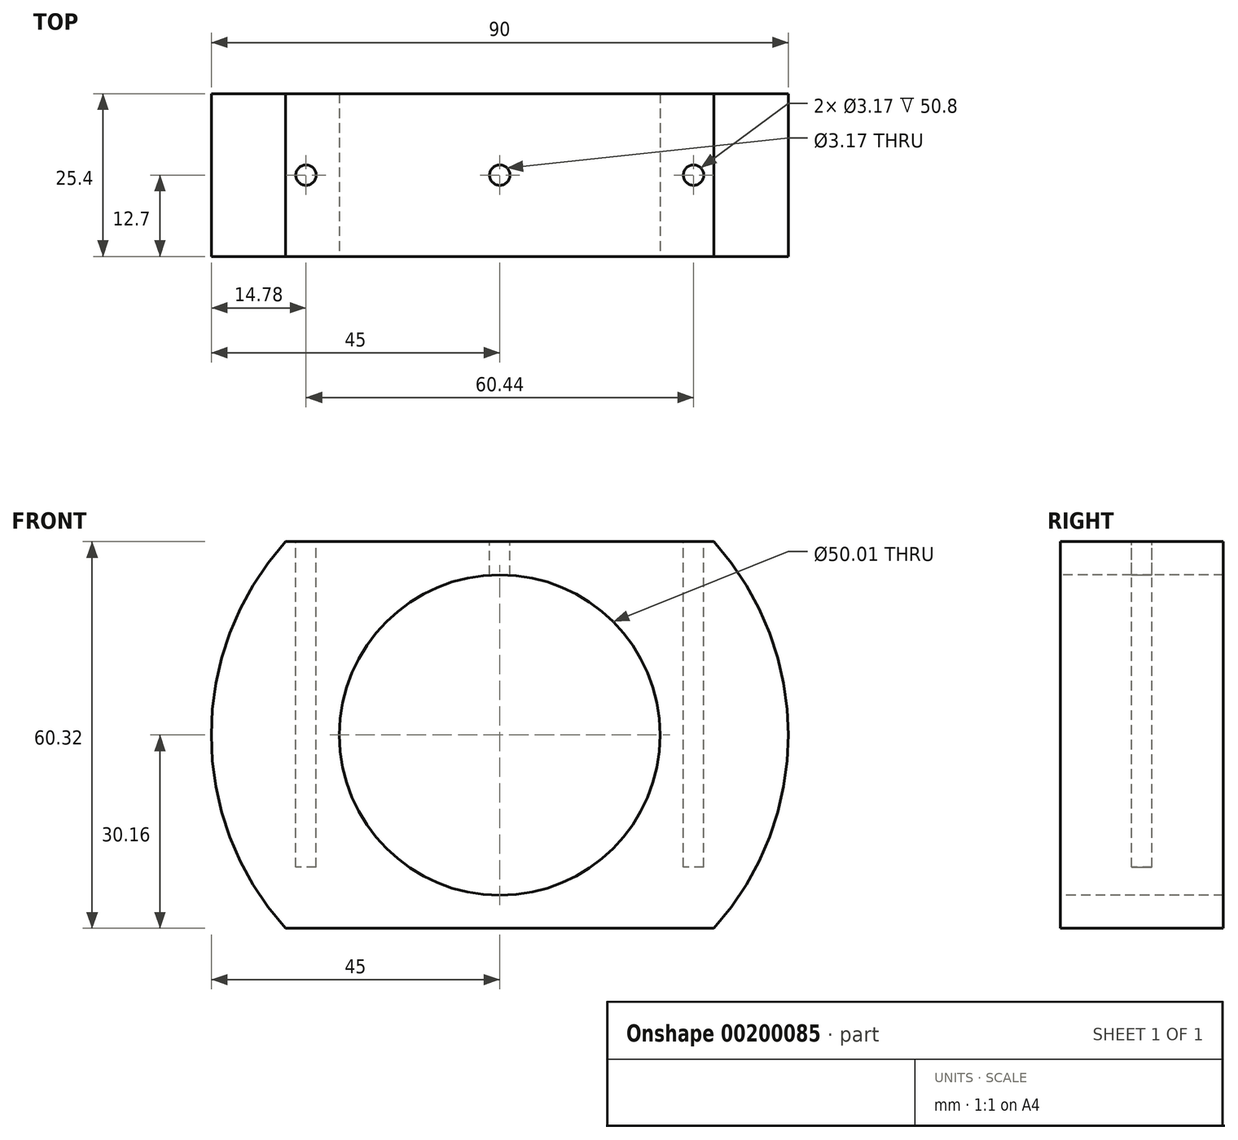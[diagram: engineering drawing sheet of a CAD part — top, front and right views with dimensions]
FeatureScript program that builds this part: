
annotation { "Feature Type Name" : "Feature", "Feature Type Description" : "" }
export const myFeature = defineFeature(function(context is Context, id is Id, definition is map)
    precondition{}
    {
        {
            var Q0;
            Q0=qCreatedBy(makeId("Front.planeOp"),FACE);
            var sketch = newSketch(context, id + "F0", { "sketchPlane" : qUnion([Q0])});
            skCircle(sketch, "E0", {"center": v(0, 0) * mm, "radius": 45 * mm});
            skSolve(sketch);
        }
        {
            var Q0;
            Q0=makeQuery(id+"F0.imprint","IMPRINT",FACE,{"disambiguationData":[TD([[makeQuery(id+"F0.imprint","IMPRINT",EDGE,{"derivedFrom":sQuery(id+"F0.wireOp",EDGE,"E0")}),1.0]])]});
            var Q1;
            Q1 = qSketchRegion(id + "F2", true);
            extrude(context, id + "F1", {"entities" : qUnion([Q0, Q1]), "endBound" : BoundingType.SYMMETRIC, "depth" : 25.4 * mm});
        }
        {
            var Q0;
            Q0=makeQuery(id+"F1.opExtrude","CAP_FACE",FACE,{"disambiguationData":[OSD([sQuery(id+"F0.wireOp",EDGE,"E0")])],"isStart":false});
            var sketch = newSketch(context, id + "F2", { "sketchPlane" : qUnion([Q0])});
            skLineSegment(sketch, "E1.bottom", {"start": v(33.4, 30.16) * mm, "end": v(-33.4, 30.16) * mm});
            skLineSegment(sketch, "E1.top", {"start": v(33.4, -30.16) * mm, "end": v(-33.4, -30.16) * mm});
            skLineSegment(sketch, "E1.left", {"start": v(33.4, 30.16) * mm, "end": v(33.4, -30.16) * mm});
            skLineSegment(sketch, "E1.right", {"start": v(-33.4, 30.16) * mm, "end": v(-33.4, -30.16) * mm});
            skPoint(sketch, "E1.middle", {"position": v(0, 0) * mm});
            skSolve(sketch);
        }
        {
            var Q0;
            {var subQ0=sQuery(id+"F2.wireOp",EDGE,"E1.bottom");Q0=makeQuery(id+"F2.imprint","IMPRINT",FACE,{"disambiguationData":[TD([[makeQuery(id+"F2.imprint","IMPRINT",EDGE,{"derivedFrom":subQ0}),-1.0]])]});}
            var Q1;
            {var subQ0=sQuery(id+"F2.wireOp",EDGE,"E1.top");Q1=makeQuery(id+"F2.imprint","IMPRINT",FACE,{"disambiguationData":[TD([[makeQuery(id+"F2.imprint","IMPRINT",EDGE,{"derivedFrom":subQ0}),1.0]])]});}
            extrude(context, id + "F3", {"entities" : qUnion([Q0, Q1]), "operationType" : NewBodyOperationType.REMOVE, "endBound" : BoundingType.THROUGH_ALL, "oppositeDirection" : true, "depth" : 25.4 * mm});
        }
        {
            var Q0;
            Q0=makeQuery(id+"F1.opExtrude","CAP_FACE",FACE,{"disambiguationData":[OSD([sQuery(id+"F0.wireOp",EDGE,"E0")])],"isStart":false});
            var sketch = newSketch(context, id + "F4", { "sketchPlane" : qUnion([Q0])});
            skCircle(sketch, "E2", {"center": v(0, 0) * mm, "radius": 25 * mm});
            skSolve(sketch);
        }
        {
            var Q0;
            Q0=makeQuery(id+"F4.imprint","IMPRINT",FACE,{"disambiguationData":[TD([[makeQuery(id+"F4.imprint","IMPRINT",EDGE,{"derivedFrom":sQuery(id+"F4.wireOp",EDGE,"E2")}),1.0]])]});
            extrude(context, id + "F5", {"entities" : qUnion([Q0]), "operationType" : NewBodyOperationType.REMOVE, "endBound" : BoundingType.THROUGH_ALL, "oppositeDirection" : true, "depth" : 25.4 * mm});
        }
        {
            var Q0;
            Q0=makeQuery(id+"F3.boolean.opBoolean","COPY",FACE,{"derivedFrom":makeQuery(id+"F3.opExtrude","SWEPT_FACE",FACE,{"disambiguationData":[OSD([sQuery(id+"F2.wireOp",EDGE,"E1.bottom")])]})});
            var sketch = newSketch(context, id + "F6", { "sketchPlane" : qUnion([Q0])});
            skCircle(sketch, "E3", {"center": v(0, 0) * mm, "radius": 1.59 * mm});
            skCircle(sketch, "E4", {"center": v(30.22, 0) * mm, "radius": 1.59 * mm});
            skCircle(sketch, "E5", {"center": v(-30.22, 0) * mm, "radius": 1.59 * mm});
            skSolve(sketch);
        }
        {
            var Q0;
            Q0=makeQuery(id+"F6.imprint","IMPRINT",FACE,{"disambiguationData":[TD([[makeQuery(id+"F6.imprint","IMPRINT",EDGE,{"derivedFrom":sQuery(id+"F6.wireOp",EDGE,"E4")}),1.0]])]});
            var Q1;
            Q1=makeQuery(id+"F6.imprint","IMPRINT",FACE,{"disambiguationData":[TD([[makeQuery(id+"F6.imprint","IMPRINT",EDGE,{"derivedFrom":sQuery(id+"F6.wireOp",EDGE,"E3")}),1.0]])]});
            var Q2;
            Q2=makeQuery(id+"F6.imprint","IMPRINT",FACE,{"disambiguationData":[TD([[makeQuery(id+"F6.imprint","IMPRINT",EDGE,{"derivedFrom":sQuery(id+"F6.wireOp",EDGE,"E5")}),1.0]])]});
            extrude(context, id + "F7", {"entities" : qUnion([Q0, Q1, Q2]), "operationType" : NewBodyOperationType.REMOVE, "oppositeDirection" : true, "depth" : 50.8 * mm});
        }
    });
